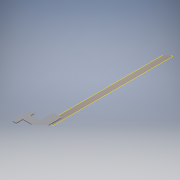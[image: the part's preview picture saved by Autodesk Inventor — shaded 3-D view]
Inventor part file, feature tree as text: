
AUTODESK INVENTOR PART (.ipt)
format: ipt  version: 2016 (Build 200138000, 138)  size: 138,752 bytes
history: native  units: mm
features: plane x1, extrude x1, fillet x1, sketch x1
ambient origin geometry x8: Origin, YZ Plane, XZ Plane, XY Plane, X Axis, Y Axis, Z Axis, Center Point
bodies: Solid1 (feature_tree)
feature tree (4):
  plane  "Work Plane1"
  extrude  "Extrusion1"  Depth=6.0mm TaperAngle=0.0deg
  fillet  "Fillet1"  Radius=92.0mm
  sketch  "Sketch1"  dims[d0=110.0mm d2=6.0mm d3=0.0mm d4=92.0mm d5=68.0mm d6=40.0mm d7=180.0mm d8=50.0mm d9=46.0mm d10=300.0mm d11=7.0mm d12=80.0mm d13=44.0mm d14=45.0mm d15=100.0mm]
